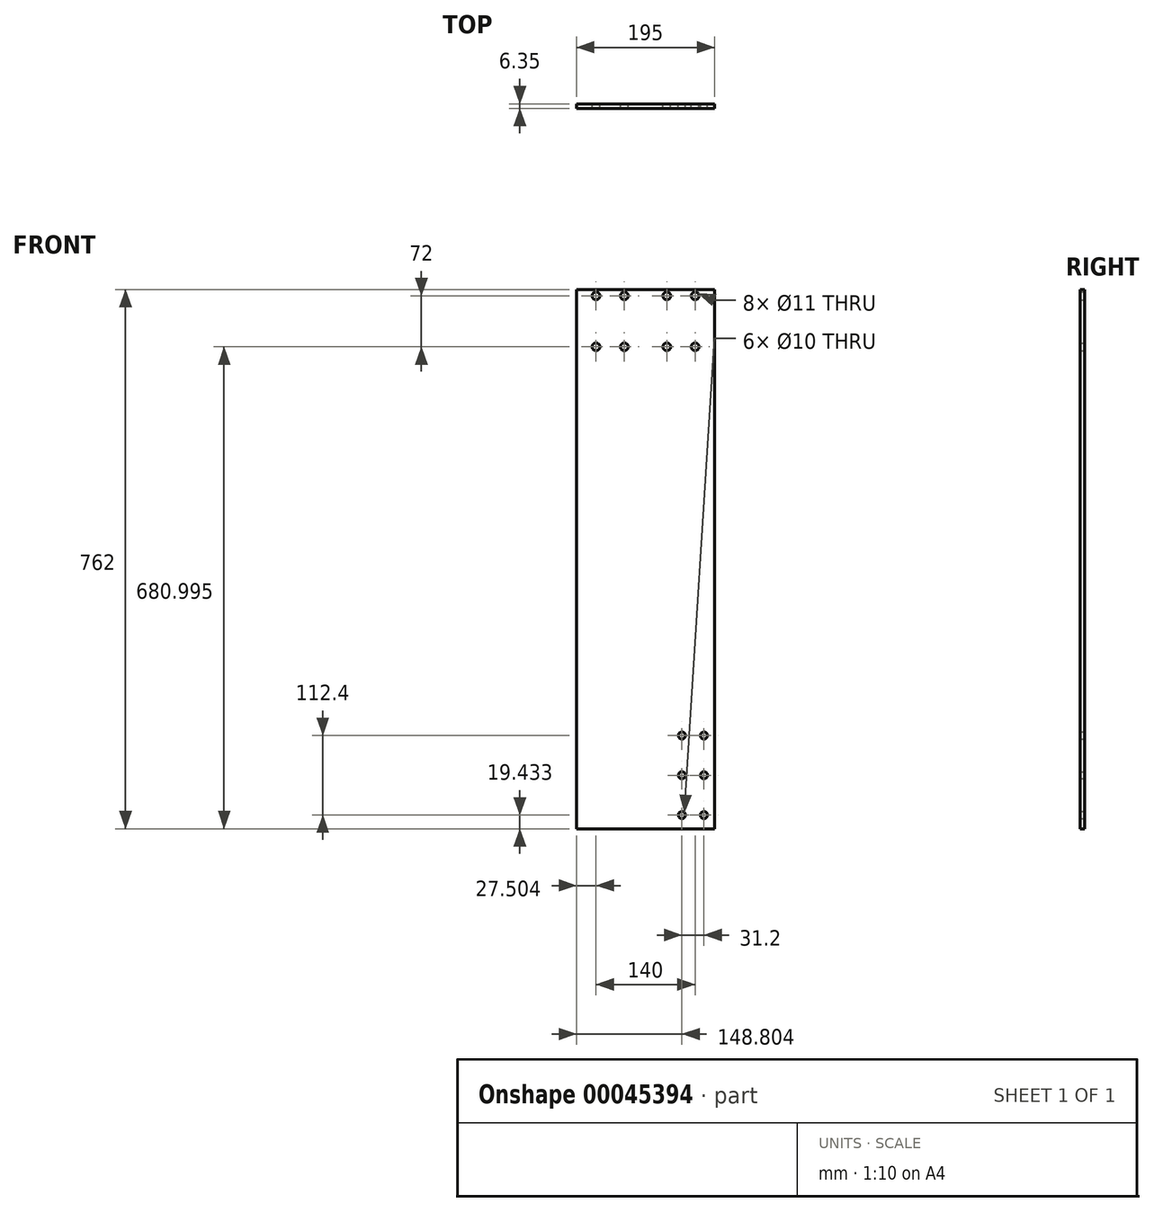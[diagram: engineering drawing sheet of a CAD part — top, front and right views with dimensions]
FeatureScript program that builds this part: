
annotation { "Feature Type Name" : "Feature", "Feature Type Description" : "" }
export const myFeature = defineFeature(function(context is Context, id is Id, definition is map)
    precondition{}
    {
        {
            var Q0;
            Q0=qCreatedBy(makeId("Front.planeOp"),FACE);
            var sketch = newSketch(context, id + "F0", { "sketchPlane" : qUnion([Q0])});
            skLineSegment(sketch, "E0.bottom", {"start": v(-74.92, 649.94) * mm, "end": v(120.08, 649.94) * mm});
            skLineSegment(sketch, "E0.top", {"start": v(-74.92, -112.06) * mm, "end": v(120.08, -112.06) * mm});
            skLineSegment(sketch, "E0.left", {"start": v(-74.92, 649.94) * mm, "end": v(-74.92, -112.06) * mm});
            skLineSegment(sketch, "E0.right", {"start": v(120.08, 649.94) * mm, "end": v(120.08, -112.06) * mm});
            skCircle(sketch, "E1", {"center": v(-47.42, 640.94) * mm, "radius": 5.5 * mm});
            skCircle(sketch, "E2", {"center": v(-47.42, 568.94) * mm, "radius": 5.5 * mm});
            skCircle(sketch, "E3", {"center": v(-7.42, 640.94) * mm, "radius": 5.5 * mm});
            skCircle(sketch, "E4", {"center": v(-7.42, 568.94) * mm, "radius": 5.5 * mm});
            skCircle(sketch, "E5", {"center": v(52.58, 640.94) * mm, "radius": 5.5 * mm});
            skCircle(sketch, "E6", {"center": v(92.58, 640.94) * mm, "radius": 5.5 * mm});
            skCircle(sketch, "E7", {"center": v(52.58, 568.94) * mm, "radius": 5.5 * mm});
            skCircle(sketch, "E8", {"center": v(92.58, 568.94) * mm, "radius": 5.5 * mm});
            skLineSegment(sketch, "E9", {"start": v(20.08, 649.94) * mm, "end": v(20.08, 533.82) * mm});
            skLineSegment(sketch, "E10", {"start": v(25.08, 649.94) * mm, "end": v(25.08, 534.12) * mm});
            skSolve(sketch);
        }
        {
            var Q0;
            Q0=makeQuery(id+"F0.imprint","IMPRINT",FACE,{"disambiguationData":[TD([[makeQuery(id+"F0.imprint","IMPRINT",EDGE,{"derivedFrom":sQuery(id+"F0.wireOp",EDGE,"E0.bottom")}),-1.0]])]});
            extrude(context, id + "F1", {"entities" : qUnion([Q0]), "depth" : 6.35 * mm});
        }
        {
            var Q0;
            Q0=makeQuery(id+"F1.opExtrude","CAP_FACE",FACE,{"disambiguationData":[OSD([sQuery(id+"F0.wireOp",EDGE,"E0.bottom"),sQuery(id+"F0.wireOp",EDGE,"E0.top"),sQuery(id+"F0.wireOp",EDGE,"E0.left"),sQuery(id+"F0.wireOp",EDGE,"E0.right"),sQuery(id+"F0.wireOp",EDGE,"E1"),sQuery(id+"F0.wireOp",EDGE,"E2"),sQuery(id+"F0.wireOp",EDGE,"E3"),sQuery(id+"F0.wireOp",EDGE,"E4"),sQuery(id+"F0.wireOp",EDGE,"E5"),sQuery(id+"F0.wireOp",EDGE,"E6"),sQuery(id+"F0.wireOp",EDGE,"E7"),sQuery(id+"F0.wireOp",EDGE,"E8")])],"isStart":true});
            var sketch = newSketch(context, id + "F2", { "sketchPlane" : qUnion([Q0])});
            skCircle(sketch, "E11", {"center": v(-105.08, -92.63) * mm, "radius": 5 * mm});
            skCircle(sketch, "E12.0.1.0", {"center": v(-105.08, -36.43) * mm, "radius": 5 * mm});
            skCircle(sketch, "E12.0.2.0", {"center": v(-105.08, 19.77) * mm, "radius": 5 * mm});
            skCircle(sketch, "E12.1.0.0", {"center": v(-73.88, -92.63) * mm, "radius": 5 * mm});
            skCircle(sketch, "E12.1.1.0", {"center": v(-73.88, -36.43) * mm, "radius": 5 * mm});
            skCircle(sketch, "E12.1.2.0", {"center": v(-73.88, 19.77) * mm, "radius": 5 * mm});
            skLineSegment(sketch, "E12.direction1", {"start": v(-105.08, -92.63) * mm, "end": v(-73.88, -92.63) * mm, "construction": true});
            skLineSegment(sketch, "E12.direction2", {"start": v(-105.08, -92.63) * mm, "end": v(-105.08, -36.43) * mm, "construction": true});
            skSolve(sketch);
        }
        {
            var Q0;
            Q0=makeQuery(id+"F2.imprint","IMPRINT",FACE,{"disambiguationData":[TD([[makeQuery(id+"F2.imprint","IMPRINT",EDGE,{"derivedFrom":sQuery(id+"F2.wireOp",EDGE,"E12.1.0.0")}),1.0]])]});
            var Q1;
            Q1=makeQuery(id+"F2.imprint","IMPRINT",FACE,{"disambiguationData":[TD([[makeQuery(id+"F2.imprint","IMPRINT",EDGE,{"derivedFrom":sQuery(id+"F2.wireOp",EDGE,"E11")}),1.0]])]});
            var Q2;
            Q2=makeQuery(id+"F2.imprint","IMPRINT",FACE,{"disambiguationData":[TD([[makeQuery(id+"F2.imprint","IMPRINT",EDGE,{"derivedFrom":sQuery(id+"F2.wireOp",EDGE,"E12.1.1.0")}),1.0]])]});
            var Q3;
            Q3=makeQuery(id+"F2.imprint","IMPRINT",FACE,{"disambiguationData":[TD([[makeQuery(id+"F2.imprint","IMPRINT",EDGE,{"derivedFrom":sQuery(id+"F2.wireOp",EDGE,"E12.0.1.0")}),1.0]])]});
            var Q4;
            Q4=makeQuery(id+"F2.imprint","IMPRINT",FACE,{"disambiguationData":[TD([[makeQuery(id+"F2.imprint","IMPRINT",EDGE,{"derivedFrom":sQuery(id+"F2.wireOp",EDGE,"E12.0.2.0")}),1.0]])]});
            var Q5;
            Q5=makeQuery(id+"F2.imprint","IMPRINT",FACE,{"disambiguationData":[TD([[makeQuery(id+"F2.imprint","IMPRINT",EDGE,{"derivedFrom":sQuery(id+"F2.wireOp",EDGE,"E12.1.2.0")}),1.0]])]});
            extrude(context, id + "F3", {"entities" : qUnion([Q0, Q1, Q2, Q3, Q4, Q5]), "operationType" : NewBodyOperationType.REMOVE, "endBound" : BoundingType.THROUGH_ALL, "oppositeDirection" : true, "depth" : 25 * mm});
        }
    });
